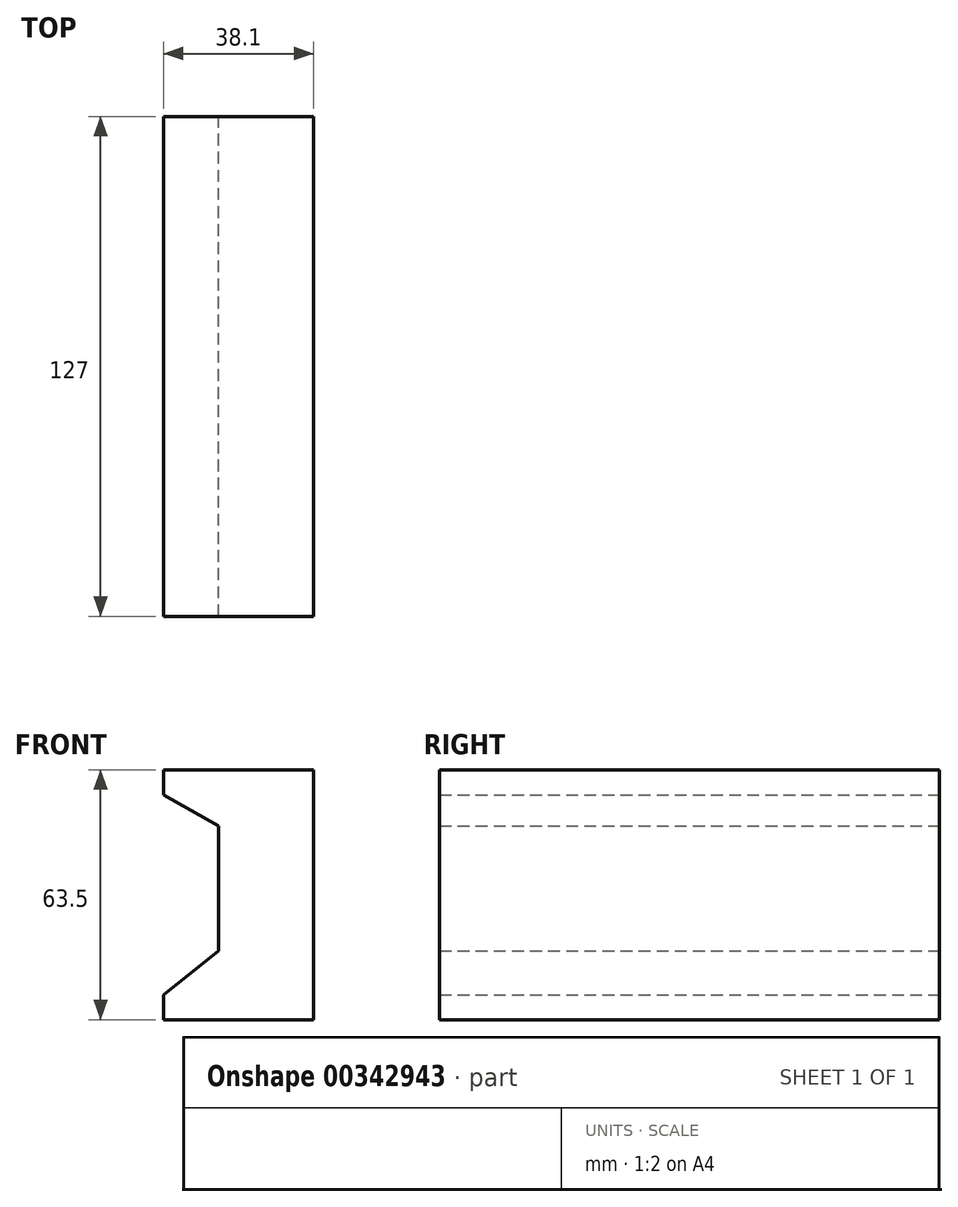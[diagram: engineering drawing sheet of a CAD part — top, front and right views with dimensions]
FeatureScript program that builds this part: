
annotation { "Feature Type Name" : "Feature", "Feature Type Description" : "" }
export const myFeature = defineFeature(function(context is Context, id is Id, definition is map)
    precondition{}
    {
        {
            var Q0;
            Q0=qCreatedBy(makeId("Front.planeOp"),FACE);
            var sketch = newSketch(context, id + "F0", { "sketchPlane" : qUnion([Q0])});
            skLineSegment(sketch, "E0", {"start": v(-34.27, 46.03) * mm, "end": v(3.83, 46.03) * mm});
            skLineSegment(sketch, "E1", {"start": v(3.83, 46.03) * mm, "end": v(3.83, -17.47) * mm});
            skLineSegment(sketch, "E2", {"start": v(3.83, -17.47) * mm, "end": v(-34.27, -17.47) * mm});
            skLineSegment(sketch, "E3", {"start": v(-34.27, 46.03) * mm, "end": v(-34.27, 39.68) * mm});
            skLineSegment(sketch, "E4", {"start": v(-34.27, -17.47) * mm, "end": v(-34.27, -11.12) * mm});
            skLineSegment(sketch, "E5", {"start": v(-34.27, -11.12) * mm, "end": v(-20.33, 0) * mm});
            skLineSegment(sketch, "E6", {"start": v(-20.33, 0) * mm, "end": v(-20.33, 31.75) * mm});
            skLineSegment(sketch, "E7", {"start": v(-34.27, 39.68) * mm, "end": v(-20.33, 31.75) * mm});
            skSolve(sketch);
        }
        {
            var Q0;
            Q0 = qSketchRegion(id + "F0", true);
            extrude(context, id + "F1", {"entities" : qUnion([Q0]), "depth" : 127 * mm});
        }
    });
